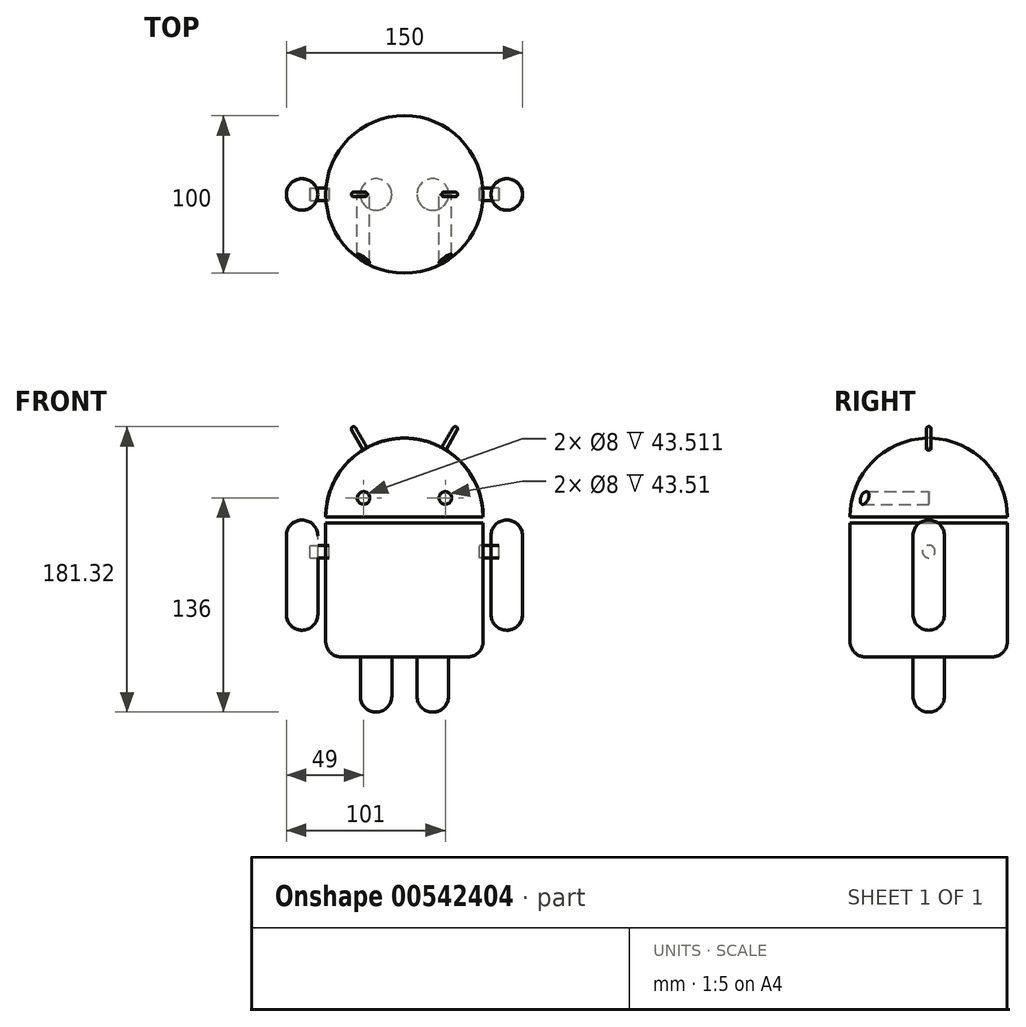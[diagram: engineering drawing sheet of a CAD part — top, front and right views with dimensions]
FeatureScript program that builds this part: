
annotation { "Feature Type Name" : "Feature", "Feature Type Description" : "" }
export const myFeature = defineFeature(function(context is Context, id is Id, definition is map)
    precondition{}
    {
        {
            var Q0;
            Q0=qCreatedBy(makeId("Front.planeOp"),FACE);
            var sketch = newSketch(context, id + "F0", { "sketchPlane" : qUnion([Q0])});
            skLineSegment(sketch, "E0", {"start": v(0, 63.5) * mm, "end": v(0, -112.89) * mm, "construction": true});
            skLineSegment(sketch, "E1", {"start": v(0, 0) * mm, "end": v(50, 0) * mm});
            skLineSegment(sketch, "E2", {"start": v(50, 0) * mm, "end": v(50, -75) * mm});
            skLineSegment(sketch, "E3", {"start": v(40, -85) * mm, "end": v(0, -85) * mm});
            skLineSegment(sketch, "E4", {"start": v(0, -85) * mm, "end": v(0, 0) * mm});
            skLineSegment(sketch, "E5", {"start": v(0, 4) * mm, "end": v(50, 4) * mm});
            skLineSegment(sketch, "E6", {"start": v(0, 4) * mm, "end": v(0, 54) * mm});
            skArc(sketch, "E7", {"start": v(50, 4) * mm, "mid": v(35.36, 39.36) * mm, "end": v(0, 54) * mm});
            skLineSegment(sketch, "E8", {"start": v(0, 54) * mm, "end": v(-42.59, 54) * mm, "construction": true});
            skPoint(sketch, "E9.visualSharp", {"position": v(50, -85) * mm});
            skArc(sketch, "E9.filletArc", {"start": v(40, -85) * mm, "mid": v(47.07, -82.07) * mm, "end": v(50, -75) * mm});
            skSolve(sketch);
        }
        {
            var Q0;
            Q0=makeQuery(id+"F0.imprint","IMPRINT",FACE,{"disambiguationData":[TD([[makeQuery(id+"F0.imprint","IMPRINT",EDGE,{"derivedFrom":sQuery(id+"F0.wireOp",EDGE,"E5")}),1.0]])]});
            var Q1;
            Q1=makeQuery(id+"F0.imprint","IMPRINT",FACE,{"disambiguationData":[TD([[makeQuery(id+"F0.imprint","IMPRINT",EDGE,{"derivedFrom":sQuery(id+"F0.wireOp",EDGE,"E1")}),-1.0]])]});
            var Q2;
            Q2=sQuery(id+"F0.wireOp",EDGE,"E0");
            revolve(context, id + "F1", {"entities" : qUnion([Q0, Q1]), "axis" : qUnion([Q2]), "revolveType" : RevolveType.FULL});
        }
        {
            var Q0;
            Q0=qCreatedBy(makeId("Front.planeOp"),FACE);
            var sketch = newSketch(context, id + "F2", { "sketchPlane" : qUnion([Q0])});
            skLineSegment(sketch, "E10", {"start": v(18, -77.06) * mm, "end": v(18, -138.1) * mm, "construction": true});
            skLineSegment(sketch, "E11", {"start": v(18, -85) * mm, "end": v(28, -85) * mm});
            skLineSegment(sketch, "E12", {"start": v(28, -85) * mm, "end": v(28, -110) * mm});
            skLineSegment(sketch, "E13", {"start": v(18, -120) * mm, "end": v(18, -120) * mm});
            skLineSegment(sketch, "E14", {"start": v(18, -120) * mm, "end": v(18, -85) * mm});
            skPoint(sketch, "E15.visualSharp", {"position": v(28, -120) * mm});
            skArc(sketch, "E15.filletArc", {"start": v(18, -120) * mm, "mid": v(25.07, -117.07) * mm, "end": v(28, -110) * mm});
            skSolve(sketch);
        }
        {
            var Q0;
            Q0=makeQuery(id+"F2.imprint","IMPRINT",FACE,{"disambiguationData":[TD([[makeQuery(id+"F2.imprint","IMPRINT",EDGE,{"derivedFrom":sQuery(id+"F2.wireOp",EDGE,"E11")}),-1.0]])]});
            var Q1;
            Q1=sQuery(id+"F2.wireOp",EDGE,"E10");
            revolve(context, id + "F3", {"operationType" : NewBodyOperationType.ADD, "entities" : qUnion([Q0]), "axis" : qUnion([Q1]), "revolveType" : RevolveType.FULL});
        }
        {
            var Q0;
            Q0=qCreatedBy(makeId("Front.planeOp"),FACE);
            var sketch = newSketch(context, id + "F4", { "sketchPlane" : qUnion([Q0])});
            skLineSegment(sketch, "E16", {"start": v(65, 12.15) * mm, "end": v(65, -85.61) * mm, "construction": true});
            skLineSegment(sketch, "E17.bottom", {"start": v(65, -68) * mm, "end": v(65, -68) * mm});
            skLineSegment(sketch, "E17.top", {"start": v(65, 2) * mm, "end": v(65, 2) * mm});
            skLineSegment(sketch, "E17.left", {"start": v(65, -68) * mm, "end": v(65, 2) * mm});
            skLineSegment(sketch, "E17.right", {"start": v(75, -58) * mm, "end": v(75, -8) * mm});
            skPoint(sketch, "E18.visualSharp", {"position": v(75, -68) * mm});
            skArc(sketch, "E18.filletArc", {"start": v(65, -68) * mm, "mid": v(72.07, -65.07) * mm, "end": v(75, -58) * mm});
            skPoint(sketch, "E19.visualSharp", {"position": v(75, 2) * mm});
            skArc(sketch, "E19.filletArc", {"start": v(75, -8) * mm, "mid": v(72.07, -0.93) * mm, "end": v(65, 2) * mm});
            skSolve(sketch);
        }
        {
            var Q0;
            Q0=qSketchRegion(id+"F4",true);
            var Q1;
            Q1=sQuery(id+"F4.wireOp",EDGE,"E16");
            revolve(context, id + "F5", {"entities" : qUnion([Q0]), "axis" : qUnion([Q1]), "revolveType" : RevolveType.FULL});
        }
        {
            var Q0;
            Q0=qCreatedBy(makeId("Front.planeOp"),FACE);
            var sketch = newSketch(context, id + "F6", { "sketchPlane" : qUnion([Q0])});
            skLineSegment(sketch, "E20", {"start": v(0, 3.96) * mm, "end": v(16.28, 32.17) * mm, "construction": true});
            skLineSegment(sketch, "E21", {"start": v(23, 43.8) * mm, "end": v(24.3, 43.05) * mm});
            skLineSegment(sketch, "E22", {"start": v(24.3, 43.05) * mm, "end": v(33.55, 59.07) * mm});
            skLineSegment(sketch, "E23", {"start": v(33, 61.12) * mm, "end": v(33, 61.12) * mm});
            skLineSegment(sketch, "E24", {"start": v(33, 61.12) * mm, "end": v(23, 43.8) * mm});
            skPoint(sketch, "E25.visualSharp", {"position": v(34.3, 60.37) * mm});
            skArc(sketch, "E25.filletArc", {"start": v(33.55, 59.07) * mm, "mid": v(33.7, 60.2) * mm, "end": v(33, 61.12) * mm});
            skSolve(sketch);
        }
        {
            var Q0;
            Q0=qSketchRegion(id+"F6",true);
            var Q1;
            Q1=sQuery(id+"F6.wireOp",EDGE,"E20");
            revolve(context, id + "F7", {"operationType" : NewBodyOperationType.ADD, "entities" : qUnion([Q0]), "axis" : qUnion([Q1]), "revolveType" : RevolveType.FULL});
        }
        {
            var Q0;
            Q0=makeQuery(id+"F5.opRevolve","SWEPT_BODY",BODY,{"disambiguationData":[OSD([sQuery(id+"F4.wireOp",EDGE,"E17.left"),sQuery(id+"F4.wireOp",EDGE,"E17.right"),sQuery(id+"F4.wireOp",EDGE,"E18.filletArc"),sQuery(id+"F4.wireOp",EDGE,"E19.filletArc")])]});
            var Q1;
            Q1=makeQuery(id+"F1.opRevolve","SWEPT_BODY",BODY,{"disambiguationData":[OSD([sQuery(id+"F0.wireOp",EDGE,"E1"),sQuery(id+"F0.wireOp",EDGE,"E2"),sQuery(id+"F0.wireOp",EDGE,"E3"),sQuery(id+"F0.wireOp",EDGE,"E4"),sQuery(id+"F0.wireOp",EDGE,"E9.filletArc")])]});
            var Q2;
            Q2=makeQuery(id+"F1.opRevolve","SWEPT_BODY",BODY,{"disambiguationData":[OSD([sQuery(id+"F0.wireOp",EDGE,"E5"),sQuery(id+"F0.wireOp",EDGE,"E6"),sQuery(id+"F0.wireOp",EDGE,"E7")])]});
            var Q3;
            Q3=qCreatedBy(makeId("Right.planeOp"),FACE);
            mirror(context, id + "F8", {"entities" : qUnion([Q0, Q1, Q2]), "mirrorPlane" : qUnion([Q3])});
        }
        {
            var Q0;
            Q0=qCreatedBy(makeId("Front.planeOp"),FACE);
            var sketch = newSketch(context, id + "F9", { "sketchPlane" : qUnion([Q0])});
            skCircle(sketch, "E26", {"center": v(26, 16) * mm, "radius": 4 * mm});
            skCircle(sketch, "E27", {"center": v(-26, 16) * mm, "radius": 4 * mm});
            skSolve(sketch);
        }
        {
            var Q0;
            Q0=qSketchRegion(id+"F9",true);
            extrude(context, id + "F10", {"entities" : qUnion([Q0]), "operationType" : NewBodyOperationType.REMOVE, "depth" : 60 * mm});
        }
        {
            var Q0;
            Q0=qCreatedBy(makeId("Right.planeOp"),FACE);
            var sketch = newSketch(context, id + "F11", { "sketchPlane" : qUnion([Q0])});
            skCircle(sketch, "E28", {"center": v(0, -18) * mm, "radius": 4 * mm});
            skSolve(sketch);
        }
        {
            var Q0;
            Q0 = qSketchRegion(id + "F11", true);
            extrude(context, id + "F12", {"entities" : qUnion([Q0]), "depth" : 60 * mm, "offsetDistance" : 25 * mm, "hasSecondDirection" : true, "secondDirectionOppositeDirection" : false, "secondDirectionDepth" : 47.8 * mm});
        }
        {
            var Q0;
            Q0=makeQuery(id+"F12.opExtrude","SWEPT_BODY",BODY,{"disambiguationData":[OSD([sQuery(id+"F11.wireOp",EDGE,"E28")])]});
            var Q1;
            Q1=qCreatedBy(makeId("Right.planeOp"),FACE);
            mirror(context, id + "F13", {"entities" : qUnion([Q0]), "mirrorPlane" : qUnion([Q1])});
        }
    });
